# Revit family: Daloc T25 snabbsortiment
name_source: partatom
category: Doors
revit_build: Autodesk Revit LT 2017 (Build: 20160225_1515(x64)
units: mm (PartAtom-declared; Revit-internal decimal feet)

## family parameters
Always vertical = Yes
Cut with Voids When Loaded = No
Host = Wall
OmniClass Number = 23.30.10.00
OmniClass Title = Doors
Room Calculation Point = No
Shared = No

## types (3) — shared parameters
Frame Projection Ext. = 25 mm  [stored 0.082021 ft]
Frame Projection Int. = 25 mm  [stored 0.082021 ft]
Frame Width = 75 mm  [stored 0.246063 ft]
Function = Interior
Height = 2100 mm
Wall Closure = By host

## per-type parameters (varying)
| type | Modulbredd | Rough Width | Width |
| 8x21 | 8 | 800 mm  [stored 2.62467 ft] | 800 mm  [stored 2.62467 ft] |
| 9x21 | 9 | 900 mm  [stored 2.95276 ft] | 900 mm  [stored 2.95276 ft] |
| 10x21 | 10 | 1000 mm  [stored 3.28084 ft] | 1000 mm  [stored 3.28084 ft] |

note: [stored X ft] marks values corroborated as IEEE doubles in the binary element streams (Revit-internal decimal feet)

## geometry (parser evidence)
native form markers: Sweep x9
no freeform markers — native parametric forms only
